# Revit family: Windows_Purso_LK90eco_Double-Sash_Inward-Opening-Tilt-Turn-Window-Without-Middle-Post
name_source: partatom
category: Windows
revit_build: Autodesk Revit 2018 (Build: 20170223_1515(x64)
units: mm (PartAtom-declared; Revit-internal decimal feet)

## family parameters
Always vertical = Yes
Cut with Voids When Loaded = No
Host = Wall
OmniClass Number = 23.30.20.00
OmniClass Title = Windows
Room Calculation Point = No
Shared = No

## types (1)
- 1000mm x 1300mm
    Analytic Construction = <None>
    Assembly Code = B2020100
    Default Sill Height = 800 mm
    Description = Thermally highly insulated Window system, inward opening
    Edition number = 1
    Frame Material = Default
    Handle Material = Aluminium - Purso - Aluminium
    Height = 1300 mm
    Keynote = 08500
    Leaf Material = Default
    Manufacturer = Purso
    Model = LK90eco inward opening (tilt/turn) window
    Product Guid = 71f55c95-27c1-41e3-a642-336d483462be
    Product data url = https://www.bimobject.com
    Type Comments = 1000mm x 1300mm
    URL = https://purso.fi
    Wall Closure = By host
    Width = 1000 mm  [stored 3.28084 ft]

note: [stored X ft] marks values corroborated as IEEE doubles in the binary element streams (Revit-internal decimal feet)

## geometry (parser evidence)
native form markers: Sweep x9
no freeform markers — native parametric forms only
